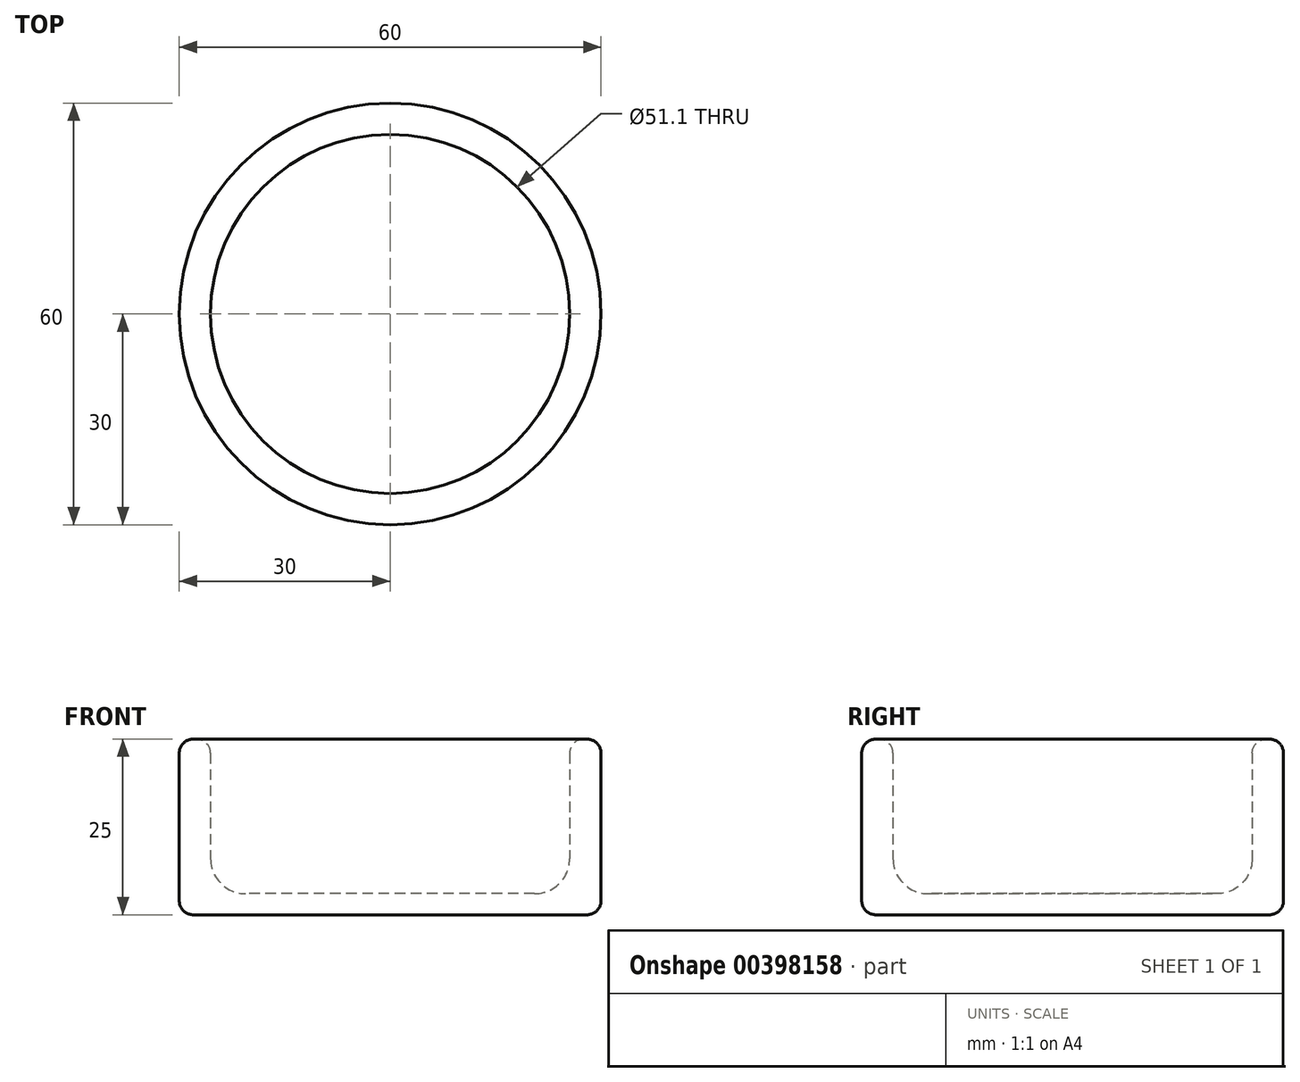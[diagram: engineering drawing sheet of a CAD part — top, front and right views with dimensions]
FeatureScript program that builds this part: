
annotation { "Feature Type Name" : "Feature", "Feature Type Description" : "" }
export const myFeature = defineFeature(function(context is Context, id is Id, definition is map)
    precondition{}
    {
        {
            var Q0;
            Q0=qCreatedBy(makeId("Top.planeOp"),FACE);
            var sketch = newSketch(context, id + "F0", { "sketchPlane" : qUnion([Q0])});
            skCircle(sketch, "E0", {"center": v(0, 0) * mm, "radius": 30 * mm});
            skCircle(sketch, "E1", {"center": v(0, 0) * mm, "radius": 25.55 * mm});
            skCircle(sketch, "E2", {"center": v(0, 0) * mm, "radius": 30.5 * mm});
            skCircle(sketch, "E3", {"center": v(0, 0) * mm, "radius": 40 * mm});
            skSolve(sketch);
        }
        {
            var Q0;
            Q0=makeQuery(id+"F0.imprint","IMPRINT",FACE,{"disambiguationData":[TD([[makeQuery(id+"F0.imprint","IMPRINT",EDGE,{"derivedFrom":sQuery(id+"F0.wireOp",EDGE,"E0")}),1.0]])]});
            var Q1;
            Q1=makeQuery(id+"F0.imprint","IMPRINT",FACE,{"disambiguationData":[TD([[makeQuery(id+"F0.imprint","IMPRINT",EDGE,{"derivedFrom":sQuery(id+"F0.wireOp",EDGE,"E1")}),1.0]])]});
            extrude(context, id + "F1", {"entities" : qUnion([Q0, Q1]), "depth" : 3 * mm});
        }
        {
            var Q0;
            Q0=makeQuery(id+"F0.imprint","IMPRINT",FACE,{"disambiguationData":[TD([[makeQuery(id+"F0.imprint","IMPRINT",EDGE,{"derivedFrom":sQuery(id+"F0.wireOp",EDGE,"E0")}),1.0]])]});
            extrude(context, id + "F2", {"entities" : qUnion([Q0]), "operationType" : NewBodyOperationType.ADD, "depth" : 25 * mm});
        }
        {
            var Q0;
            Q0=makeQuery(id+"F2.boolean.opBoolean","INTERSECT",EDGE,{"derivedFrom":[makeQuery(id+"F1.opExtrude","CAP_FACE",FACE,{"disambiguationData":[OSD([sQuery(id+"F0.wireOp",EDGE,"E0")])],"isStart":false}),makeQuery(id+"F2.opExtrude","SWEPT_FACE",FACE,{"disambiguationData":[OSD([sQuery(id+"F0.wireOp",EDGE,"E1")])]})]});
            fillet(context, id + "F3", {"entities" : qUnion([Q0]), "radius" : 5 * mm, "tangentPropagation" : true, "allowEdgeOverflow" : false});
        }
        {
            var Q0;
            Q0=makeQuery(id+"F2.opExtrude","CAP_EDGE",EDGE,{"disambiguationData":[OSD([sQuery(id+"F0.wireOp",EDGE,"E1")])],"isStart":false});
            var Q1;
            Q1=makeQuery(id+"F2.opExtrude","CAP_EDGE",EDGE,{"disambiguationData":[OSD([sQuery(id+"F0.wireOp",EDGE,"E0")])],"isStart":false});
            fillet(context, id + "F4", {"entities" : qUnion([Q0, Q1]), "radius" : 2 * mm, "tangentPropagation" : true, "allowEdgeOverflow" : false});
        }
        {
            var Q0;
            Q0=makeQuery(id+"F0.imprint","IMPRINT",FACE,{"disambiguationData":[TD([[makeQuery(id+"F0.imprint","IMPRINT",EDGE,{"derivedFrom":sQuery(id+"F0.wireOp",EDGE,"E2")}),-1.0]])]});
            extrude(context, id + "F5", {"entities" : qUnion([Q0]), "operationType" : NewBodyOperationType.REMOVE, "depth" : 27.3 * mm, "offsetDistance" : 25 * mm});
        }
        {
            var Q0;
            Q0=makeQuery(id+"F1.opExtrude","CAP_EDGE",EDGE,{"disambiguationData":[OSD([sQuery(id+"F0.wireOp",EDGE,"E0")])],"isStart":true});
            fillet(context, id + "F6", {"entities" : qUnion([Q0]), "radius" : 2 * mm, "tangentPropagation" : true, "allowEdgeOverflow" : false});
        }
    });
